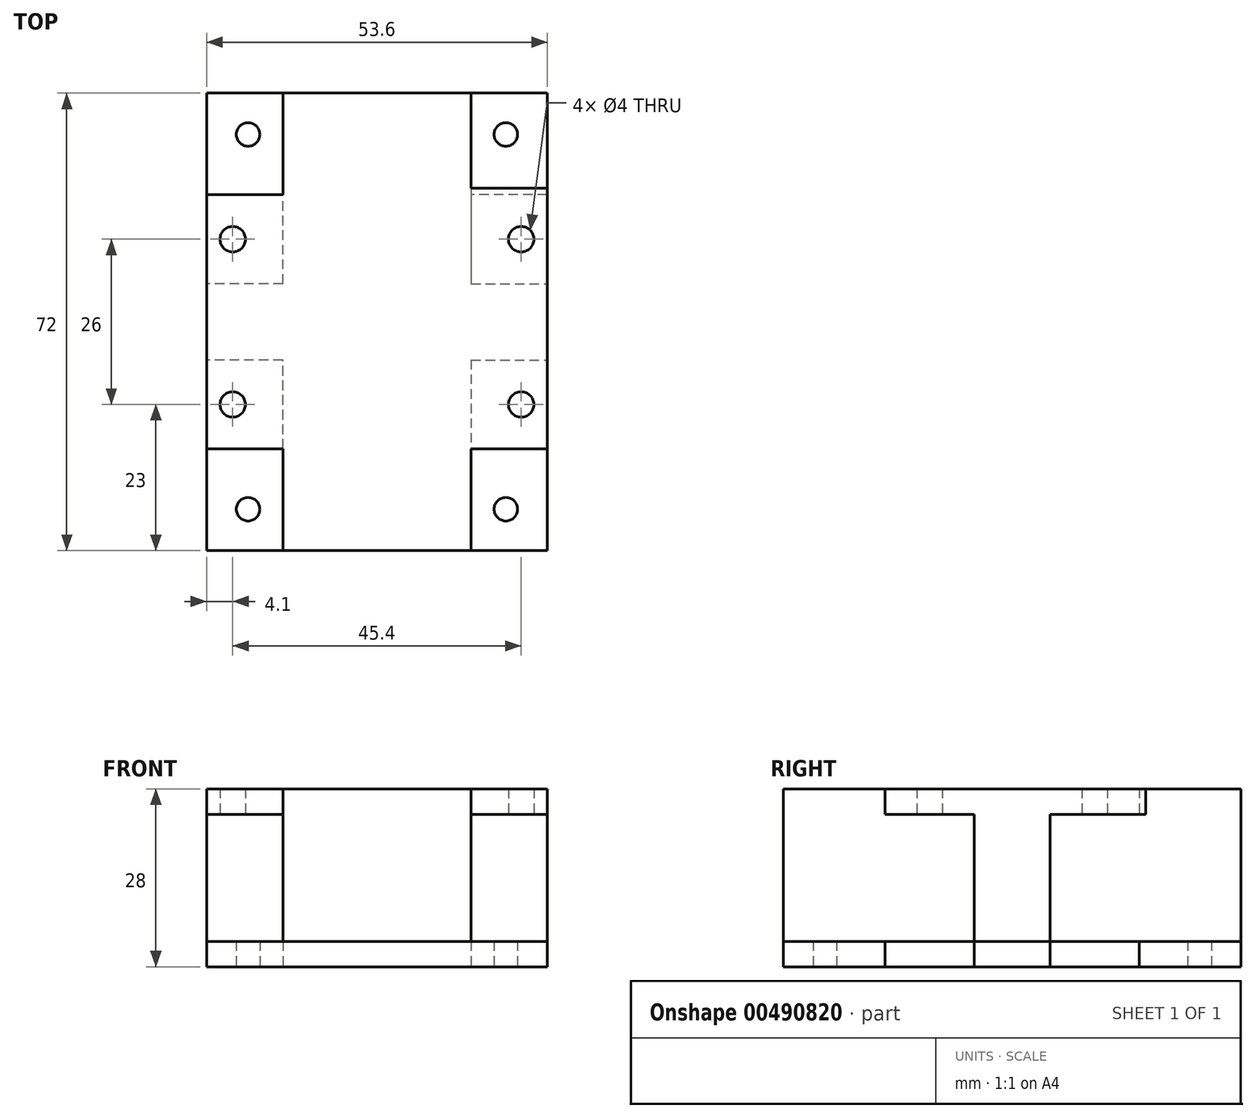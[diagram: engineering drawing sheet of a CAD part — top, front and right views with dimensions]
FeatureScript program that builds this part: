
annotation { "Feature Type Name" : "Feature", "Feature Type Description" : "" }
export const myFeature = defineFeature(function(context is Context, id is Id, definition is map)
    precondition{}
    {
        {
            var Q0;
            Q0=qCreatedBy(makeId("Top.planeOp"),FACE);
            var sketch = newSketch(context, id + "F0", { "sketchPlane" : qUnion([Q0])});
            skLineSegment(sketch, "E0.bottom", {"start": v(26.8, 36) * mm, "end": v(-26.8, 36) * mm});
            skLineSegment(sketch, "E0.top", {"start": v(26.8, -36) * mm, "end": v(-26.8, -36) * mm});
            skLineSegment(sketch, "E0.left", {"start": v(26.8, 36) * mm, "end": v(26.8, 20) * mm});
            skLineSegment(sketch, "E0.right", {"start": v(-26.8, 36) * mm, "end": v(-26.8, 20) * mm});
            skPoint(sketch, "E0.middle", {"position": v(0, 0) * mm});
            skLineSegment(sketch, "E1", {"start": v(-26.8, 0) * mm, "end": v(26.8, 0) * mm, "construction": true});
            skLineSegment(sketch, "E2", {"start": v(0, 36) * mm, "end": v(0, -36) * mm, "construction": true});
            skCircle(sketch, "E3.MirrorC", {"center": v(-20.29, 29.49) * mm, "radius": 1.85 * mm});
            skCircle(sketch, "E4.MirrorC", {"center": v(20.29, 29.49) * mm, "radius": 1.85 * mm});
            skLineSegment(sketch, "E5.MirrorCS", {"start": v(0, -36) * mm, "end": v(0, 36) * mm, "construction": true});
            skCircle(sketch, "E6.MirrorC", {"center": v(-20.29, -29.49) * mm, "radius": 1.85 * mm});
            skCircle(sketch, "E7.MirrorC", {"center": v(20.29, -29.49) * mm, "radius": 1.85 * mm});
            skLineSegment(sketch, "E8", {"start": v(26.8, -20) * mm, "end": v(14.8, -20) * mm});
            skLineSegment(sketch, "E9", {"start": v(14.8, -20) * mm, "end": v(14.8, -6) * mm});
            skLineSegment(sketch, "E10", {"start": v(14.8, -6) * mm, "end": v(26.8, -6) * mm});
            skLineSegment(sketch, "E11.trimOffspring", {"start": v(26.8, -20) * mm, "end": v(26.8, -36) * mm});
            skLineSegment(sketch, "E12.MirrorCS", {"start": v(-26.8, -20) * mm, "end": v(-14.8, -20) * mm});
            skLineSegment(sketch, "E13.MirrorCS", {"start": v(-14.8, -20) * mm, "end": v(-14.8, -6) * mm});
            skLineSegment(sketch, "E14.MirrorCS", {"start": v(-14.8, -6) * mm, "end": v(-26.8, -6) * mm});
            skLineSegment(sketch, "E15.trimOffspring", {"start": v(-26.8, -20) * mm, "end": v(-26.8, -36) * mm});
            skLineSegment(sketch, "E16.MirrorCS", {"start": v(-14.8, 20) * mm, "end": v(-14.8, 6) * mm});
            skLineSegment(sketch, "E17.MirrorCS", {"start": v(-14.8, 6) * mm, "end": v(-26.8, 6) * mm});
            skLineSegment(sketch, "E18.MirrorCS", {"start": v(-26.8, 20) * mm, "end": v(-14.8, 20) * mm});
            skLineSegment(sketch, "E19.MirrorCS", {"start": v(14.8, 20) * mm, "end": v(14.8, 6) * mm});
            skLineSegment(sketch, "E20.MirrorCS", {"start": v(26.8, 20) * mm, "end": v(14.8, 20) * mm});
            skLineSegment(sketch, "E21.MirrorCS", {"start": v(14.8, 6) * mm, "end": v(26.8, 6) * mm});
            skLineSegment(sketch, "E22.trimOffspring", {"start": v(-26.8, 6) * mm, "end": v(-26.8, -6) * mm});
            skLineSegment(sketch, "E23.trimOffspring", {"start": v(26.8, 6) * mm, "end": v(26.8, -6) * mm});
            skSolve(sketch);
        }
        {
            var Q0;
            Q0 = qSketchRegion(id + "F0", true);
            extrude(context, id + "F1", {"entities" : qUnion([Q0]), "offsetDistance" : 25 * mm, "depth" : 4 * mm});
        }
        {
            var Q0;
            Q0=makeQuery(id+"F1.opExtrude","CAP_FACE",FACE,{"disambiguationData":[OSD([sQuery(id+"F0.wireOp",EDGE,"dade2292-9b36-4658-a6cf-03d2bdeb0399.0"),sQuery(id+"F0.wireOp",EDGE,"dade2292-9b36-4658-a6cf-03d2bdeb0399.1"),sQuery(id+"F0.wireOp",EDGE,"dade2292-9b36-4658-a6cf-03d2bdeb0399.2"),sQuery(id+"F0.wireOp",EDGE,"dade2292-9b36-4658-a6cf-03d2bdeb0399.3"),sQuery(id+"F0.wireOp",EDGE,"dade2292-9b36-4658-a6cf-03d2bdeb0399.4"),sQuery(id+"F0.wireOp",EDGE,"dade2292-9b36-4658-a6cf-03d2bdeb0399.5"),sQuery(id+"F0.wireOp",EDGE,"32d030c6-2377-41f6-9b63-d697d0291395.MirrorCS"),sQuery(id+"F0.wireOp",EDGE,"a97e7850-83e3-40cb-ad54-08c425bb5fd4.MirrorCS"),sQuery(id+"F0.wireOp",EDGE,"6bfb8402-97e5-4e31-b66c-5f20c311682f.MirrorCS"),sQuery(id+"F0.wireOp",EDGE,"517f1500-328e-45ed-b509-f32702dadfd7.MirrorCS"),sQuery(id+"F0.wireOp",EDGE,"e7fb774d-d3c1-46f2-a91b-4b1a0a5a1333.MirrorCS"),sQuery(id+"F0.wireOp",EDGE,"edbffab4-3338-46f5-88c6-a7fbfea4c497.MirrorCS"),sQuery(id+"F0.wireOp",EDGE,"8406598f-176e-4762-9169-811925971b8f.MirrorCS"),sQuery(id+"F0.wireOp",EDGE,"95119a27-5dfa-476f-85cc-1f9af526979d.MirrorCS"),sQuery(id+"F0.wireOp",EDGE,"9c579885-7e13-48c1-9c92-0a85655d938f.MirrorCS"),sQuery(id+"F0.wireOp",EDGE,"a876e00e-b958-4fcb-a05d-dd2fcdcb8b96.MirrorCS"),sQuery(id+"F0.wireOp",EDGE,"aed8054b-9f59-4b14-9d8d-5be1e8eab46b.MirrorCS"),sQuery(id+"F0.wireOp",EDGE,"8091c98f-32a5-48da-977e-e035e32bc1cb.MirrorCS"),sQuery(id+"F0.wireOp",EDGE,"a8709a57-5a7f-4a95-a5ae-b77be4250be7.MirrorCS"),sQuery(id+"F0.wireOp",EDGE,"b48e5149-f646-4c17-b375-0b23445c6a29.MirrorCS"),sQuery(id+"F0.wireOp",EDGE,"a4ceddc3-f49b-4da0-8024-a1495ef9f282.MirrorCS"),sQuery(id+"F0.wireOp",EDGE,"b5320e0d-4dd0-4043-a5c0-6c7d2ce7dec5.MirrorCS"),sQuery(id+"F0.wireOp",EDGE,"b3cd8e9e-16c8-41ec-ad74-f873e9879f54.MirrorCS"),sQuery(id+"F0.wireOp",EDGE,"96f286df-436a-4ec2-9299-46ff5be35d7b.MirrorCS"),sQuery(id+"F0.wireOp",EDGE,"E3.MirrorC"),sQuery(id+"F0.wireOp",EDGE,"E4.MirrorC"),sQuery(id+"F0.wireOp",EDGE,"E0.bottom"),sQuery(id+"F0.wireOp",EDGE,"E0.top"),sQuery(id+"F0.wireOp",EDGE,"E0.left"),sQuery(id+"F0.wireOp",EDGE,"E0.right"),sQuery(id+"F0.wireOp",EDGE,"E6.MirrorC"),sQuery(id+"F0.wireOp",EDGE,"E7.MirrorC")])],"isStart":false});
            var sketch = newSketch(context, id + "F2", { "sketchPlane" : qUnion([Q0])});
            skLineSegment(sketch, "E24.bottom", {"start": v(14.8, 36) * mm, "end": v(-14.8, 36) * mm});
            skPoint(sketch, "E24.middle", {"position": v(0.27, -0.15) * mm});
            skLineSegment(sketch, "E25", {"start": v(26.8, -6) * mm, "end": v(14.8, -6) * mm});
            skLineSegment(sketch, "E26", {"start": v(14.8, -6) * mm, "end": v(14.8, -36) * mm});
            skLineSegment(sketch, "E27", {"start": v(14.8, -36) * mm, "end": v(-14.8, -36) * mm});
            skLineSegment(sketch, "E28", {"start": v(-14.8, -6) * mm, "end": v(-26.8, -6) * mm});
            skLineSegment(sketch, "E29", {"start": v(-26.8, -6) * mm, "end": v(-26.8, 6) * mm});
            skLineSegment(sketch, "E30", {"start": v(-26.8, 6) * mm, "end": v(-14.8, 6) * mm});
            skLineSegment(sketch, "E31", {"start": v(-14.8, 6) * mm, "end": v(-14.8, 36) * mm});
            skLineSegment(sketch, "E32", {"start": v(-14.8, 36) * mm, "end": v(14.8, 36) * mm});
            skLineSegment(sketch, "E33", {"start": v(14.8, 36) * mm, "end": v(14.8, 6) * mm});
            skLineSegment(sketch, "E34", {"start": v(14.8, 6) * mm, "end": v(26.8, 6) * mm});
            skLineSegment(sketch, "E35", {"start": v(-14.8, -36) * mm, "end": v(-14.8, -6) * mm});
            skSolve(sketch);
        }
        {
            var Q0;
            {var subQ6=sQuery(id+"F2.wireOp",EDGE,"E25");Q0=makeQuery(id+"F2.imprint","IMPRINT",FACE,{"disambiguationData":[TD([[makeQuery(id+"F2.imprint","IMPRINT",EDGE,{"derivedFrom":subQ6}),1.0]])]});}
            extrude(context, id + "F3", {"entities" : qUnion([Q0]), "depth" : 20 * mm, "offsetDistance" : 25 * mm});
        }
        {
            var Q0;
            Q0=makeQuery(id+"F3.opExtrude","CAP_FACE",FACE,{"disambiguationData":[OSD([sQuery(id+"F0.wireOp",EDGE,"E23.trimOffspring"),sQuery(id+"F2.wireOp",EDGE,"E25"),sQuery(id+"F2.wireOp",EDGE,"E26"),sQuery(id+"F2.wireOp",EDGE,"E27"),sQuery(id+"F2.wireOp",EDGE,"E28"),sQuery(id+"F2.wireOp",EDGE,"E29"),sQuery(id+"F2.wireOp",EDGE,"E30"),sQuery(id+"F2.wireOp",EDGE,"E31"),sQuery(id+"F2.wireOp",EDGE,"E32"),sQuery(id+"F2.wireOp",EDGE,"E33"),sQuery(id+"F2.wireOp",EDGE,"E34"),sQuery(id+"F2.wireOp",EDGE,"E35")])],"isStart":false});
            var sketch = newSketch(context, id + "F4", { "sketchPlane" : qUnion([Q0])});
            skLineSegment(sketch, "E36.bottom", {"start": v(14.8, -36) * mm, "end": v(-14.8, -36) * mm});
            skLineSegment(sketch, "E36.top", {"start": v(14.8, 36) * mm, "end": v(-14.8, 36) * mm});
            skLineSegment(sketch, "E36.right", {"start": v(-26.8, -20) * mm, "end": v(-26.8, 20) * mm});
            skLineSegment(sketch, "E37", {"start": v(26.8, 21) * mm, "end": v(26.8, -20) * mm});
            skLineSegment(sketch, "E38", {"start": v(26.8, -20) * mm, "end": v(14.8, -20) * mm});
            skLineSegment(sketch, "E39", {"start": v(14.8, -20) * mm, "end": v(14.8, -36) * mm});
            skLineSegment(sketch, "E40", {"start": v(14.8, 36) * mm, "end": v(14.8, 21) * mm});
            skLineSegment(sketch, "E41", {"start": v(14.8, 21) * mm, "end": v(26.8, 21) * mm});
            skLineSegment(sketch, "E42", {"start": v(-14.8, 36) * mm, "end": v(-14.8, 20) * mm});
            skLineSegment(sketch, "E43", {"start": v(-14.8, -36) * mm, "end": v(-14.8, -20) * mm});
            skLineSegment(sketch, "E44", {"start": v(-14.8, -20) * mm, "end": v(-26.8, -20) * mm});
            skLineSegment(sketch, "E45", {"start": v(-14.8, 20) * mm, "end": v(-26.8, 20) * mm});
            skCircle(sketch, "E46", {"center": v(22.7, -13) * mm, "radius": 2 * mm});
            skCircle(sketch, "E47.MirrorC", {"center": v(-22.7, -13) * mm, "radius": 2 * mm});
            skCircle(sketch, "E48.MirrorC", {"center": v(-22.7, 13) * mm, "radius": 2 * mm});
            skCircle(sketch, "E49.MirrorC", {"center": v(22.7, 13) * mm, "radius": 2 * mm});
            skSolve(sketch);
        }
        {
            var Q0;
            Q0 = qSketchRegion(id + "F4", true);
            extrude(context, id + "F5", {"entities" : qUnion([Q0]), "operationType" : NewBodyOperationType.ADD, "depth" : 4 * mm, "offsetDistance" : 25 * mm});
        }
    });
